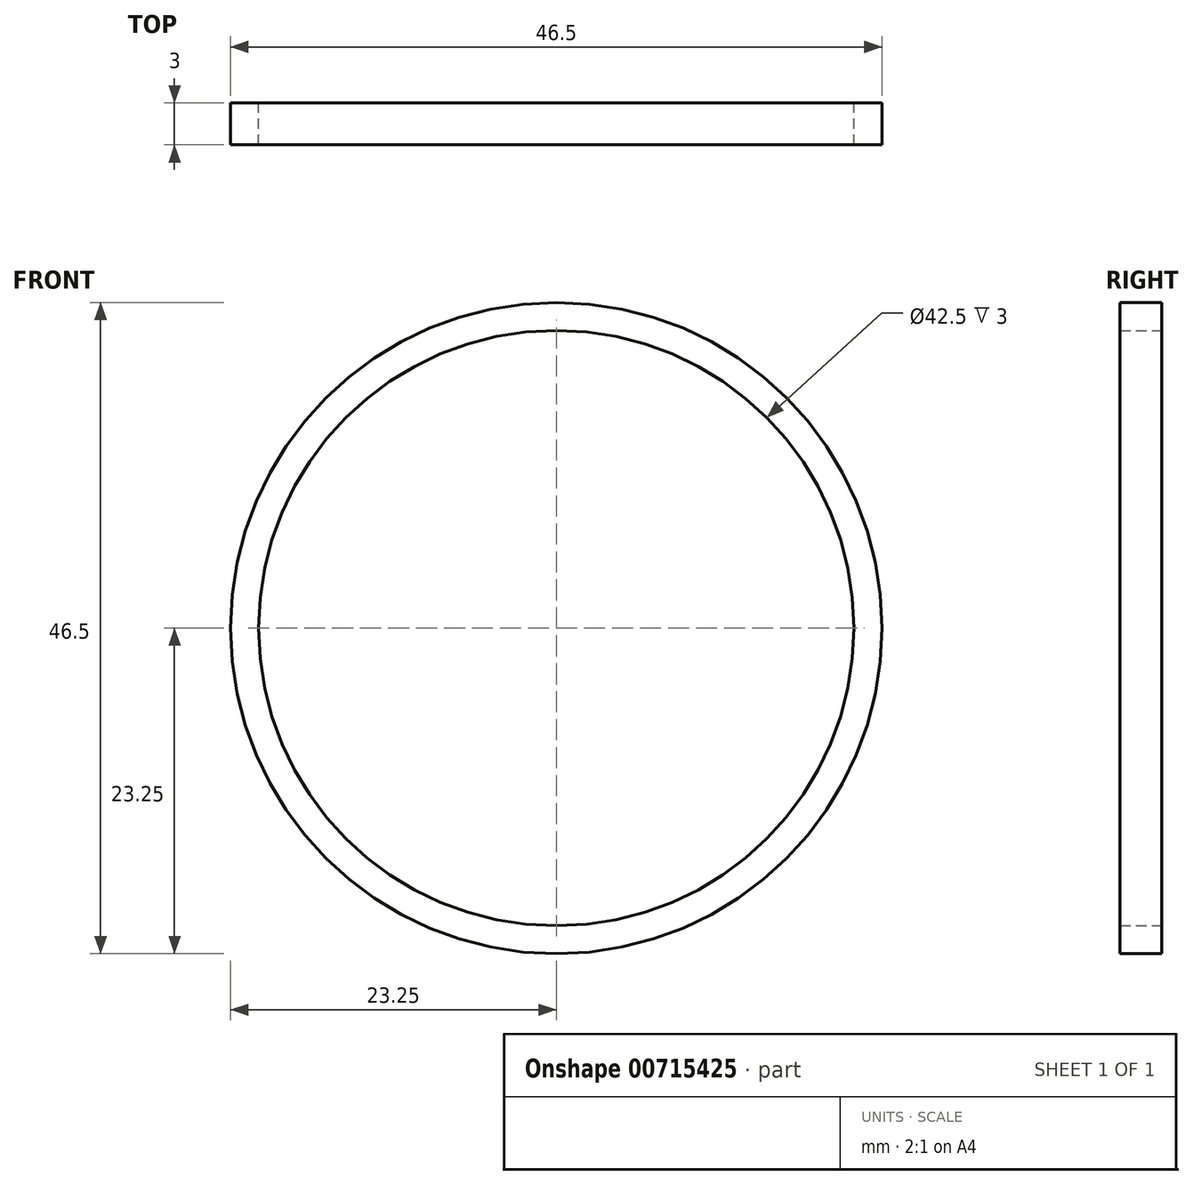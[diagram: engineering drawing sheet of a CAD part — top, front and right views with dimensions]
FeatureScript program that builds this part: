
annotation { "Feature Type Name" : "Feature", "Feature Type Description" : "" }
export const myFeature = defineFeature(function(context is Context, id is Id, definition is map)
    precondition{}
    {
        {
            var Q0;
            Q0=qCreatedBy(makeId("Front.planeOp"),FACE);
            var sketch = newSketch(context, id + "F0", { "sketchPlane" : qUnion([Q0])});
            skCircle(sketch, "E0", {"center": v(0, 0) * mm, "radius": 23.25 * mm});
            skCircle(sketch, "E1", {"center": v(0, 0) * mm, "radius": 21.25 * mm});
            skSolve(sketch);
        }
        {
            var Q0;
            Q0 = qSketchRegion(id + "F0", true);
            extrude(context, id + "F1", {"entities" : qUnion([Q0]), "depth" : 3 * mm, "offsetDistance" : 25 * mm});
        }
    });
